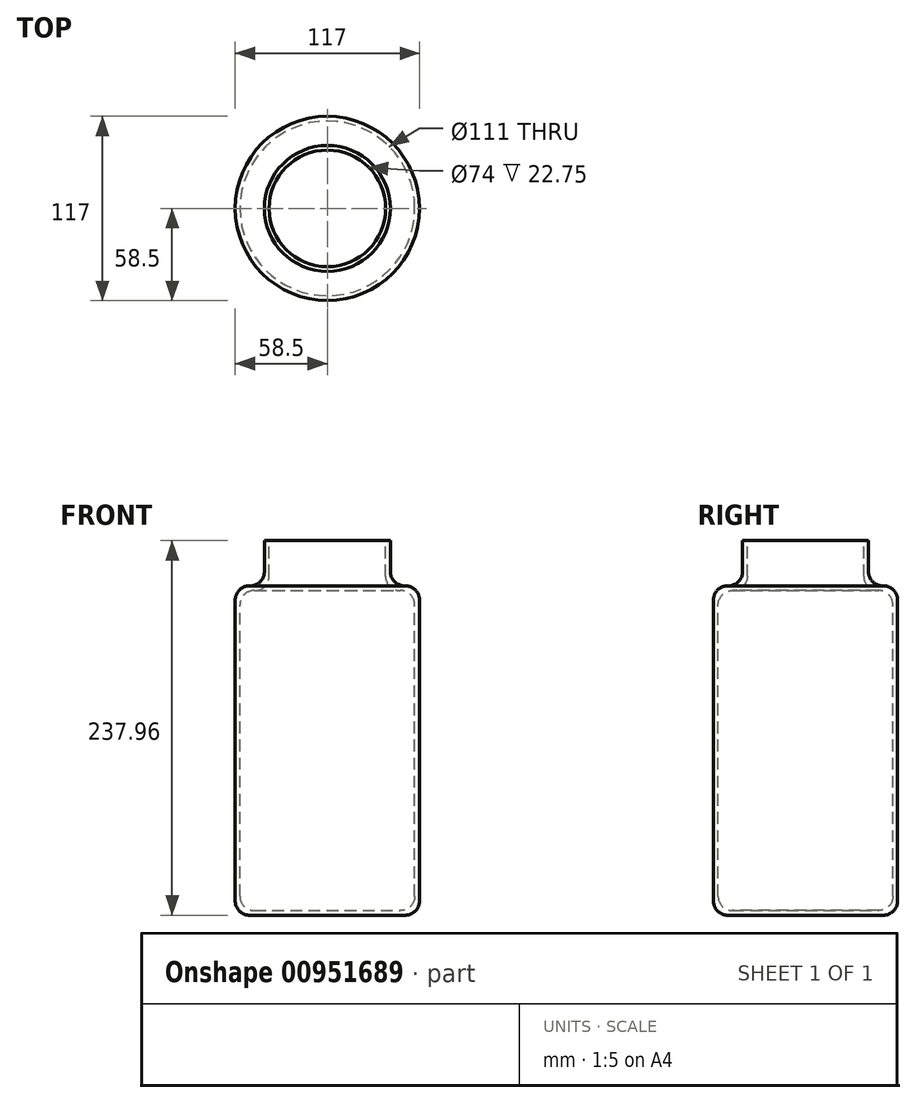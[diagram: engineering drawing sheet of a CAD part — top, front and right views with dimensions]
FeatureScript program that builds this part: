
annotation { "Feature Type Name" : "Feature", "Feature Type Description" : "" }
export const myFeature = defineFeature(function(context is Context, id is Id, definition is map)
    precondition{}
    {
        {
            var Q0;
            Q0=qCreatedBy(makeId("Right.planeOp"),FACE);
            var sketch = newSketch(context, id + "F0", { "sketchPlane" : qUnion([Q0])});
            skLineSegment(sketch, "E0", {"start": v(0, 117.48) * mm, "end": v(0, -117.48) * mm, "construction": true});
            skLineSegment(sketch, "E1", {"start": v(-37, 117.47) * mm, "end": v(-37, 85.73) * mm});
            skLineSegment(sketch, "E2", {"start": v(-55.5, 85.72) * mm, "end": v(-55.5, -117.48) * mm});
            skLineSegment(sketch, "E3", {"start": v(-55.5, -117.48) * mm, "end": v(0, -117.48) * mm});
            skLineSegment(sketch, "E4", {"start": v(-55.5, 85.72) * mm, "end": v(-37, 85.72) * mm});
            skLineSegment(sketch, "E5.0", {"start": v(-58.5, -120.48) * mm, "end": v(0, -120.48) * mm});
            skLineSegment(sketch, "E5.1", {"start": v(-58.5, 88.73) * mm, "end": v(-58.5, -120.48) * mm});
            skLineSegment(sketch, "E5.2", {"start": v(-58.5, 88.73) * mm, "end": v(-40, 88.73) * mm});
            skLineSegment(sketch, "E5.3", {"start": v(-40, 117.47) * mm, "end": v(-40, 88.73) * mm});
            skLineSegment(sketch, "E6", {"start": v(-40, 117.48) * mm, "end": v(-37, 117.48) * mm});
            skLineSegment(sketch, "E7", {"start": v(0, -117.48) * mm, "end": v(0, -120.48) * mm});
            skSolve(sketch);
        }
        {
            var Q0;
            Q0 = qSketchRegion(id + "F0", true);
            var Q1;
            Q1=sQuery(id+"F0.wireOp",EDGE,"E0");
            revolve(context, id + "F1", {"surfaceOperationType" : NewSurfaceOperationType.NEW, "entities" : qUnion([Q0]), "axis" : qUnion([Q1]), "revolveType" : RevolveType.FULL});
        }
        {
            var Q0;
            Q0=makeQuery(id+"F1.opRevolve","SWEPT_FACE",FACE,{"disambiguationData":[OSD([sQuery(id+"F0.wireOp",EDGE,"E4")])]});
            var Q1;
            Q1=makeQuery(id+"F1.opRevolve","SWEPT_FACE",FACE,{"disambiguationData":[OSD([sQuery(id+"F0.wireOp",EDGE,"E5.2")])]});
            var Q2;
            Q2=makeQuery(id+"F1.opRevolve","SWEPT_FACE",FACE,{"disambiguationData":[OSD([sQuery(id+"F0.wireOp",EDGE,"E5.0")])]});
            var Q3;
            Q3=makeQuery(id+"F1.opRevolve","SWEPT_FACE",FACE,{"disambiguationData":[OSD([sQuery(id+"F0.wireOp",EDGE,"E3")])]});
            fillet(context, id + "F2", {"entities" : qUnion([Q0, Q1, Q2, Q3]), "radius" : 9 * mm, "tangentPropagation" : true, "allowEdgeOverflow" : false});
        }
    });
